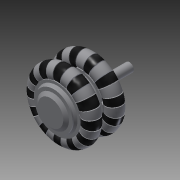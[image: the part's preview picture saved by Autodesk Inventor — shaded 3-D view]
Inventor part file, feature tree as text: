
AUTODESK INVENTOR PART (.ipt)
format: ipt  version: 2015 (Build 190159000, 159)  size: 1,335,808 bytes
history: native  units: in
note: dims shown in document units (in); Inventor stores cm internally (conversion verified against a paired STEP export)
features: sketch x14, plane x7, revolve x6, pattern_circular x3, extrude x3, mirror x1, loft x1
ambient origin geometry x8: Origin, YZ Plane, XZ Plane, XY Plane, X Axis, Y Axis, Z Axis, Center Point
bodies: Solid1 (feature_tree)
feature tree (35):
  revolve  "Revolution1"  [1 undecoded]
  revolve  "Revolution2"  [1 undecoded]
  pattern_circular  "Circular Pattern1"  Count=12 Angle=360.0deg
  sketch  "Sketch3"  dims[d7=0.0039in]
  revolve  "Revolution3"  [1 undecoded]
  sketch  "Sketch5"  dims[d9=0.0157in]
  plane  "Work Plane2"
  plane  "Work Plane6"
  revolve  "Revolution4"  Angle=360.0deg
  plane  "Work Plane4"
  revolve  "Revolution5"  [1 undecoded]
  pattern_circular  "Circular Pattern2"  [2 undecoded]
  plane  "Work Plane5"
  revolve  "Revolution6"  [1 undecoded]
  extrude  "Extrusion1"  Depth=0.0079in
  extrude  "Extrusion2"  Depth=0.3937in TaperAngle=0.0deg
  pattern_circular  "Circular Pattern3"  Count=6 Angle=360.0deg
  plane  "Work Plane7"
  mirror  "Mirror1"
  plane  "Work Plane8"
  extrude  "Extrusion3"  Depth=0.0079in
  sketch  "Sketch14"  dims[d25=0.0276in]
  plane  "Work Plane9"
  sketch  "Sketch15"  dims[d26=0.0354in]
  loft  "Loft1"
  sketch  "Sketch1"  dims[d0=0.0984in d2=0.0197in]
  sketch  "Sketch2"  dims[d5=0.0079in d6=0.0079in]
  sketch  "Sketch4"  dims[d8=90.0deg]
  sketch  "Sketch7"  dims[d10=0.0315in]
  sketch  "Sketch9"  dims[d11=15.0deg d12=4.7244in d13=360.0deg]
  sketch  "Sketch10"  dims[d15=15.0deg d17=0.0962in]
  sketch  "Sketch11"  dims[d18=0.0893in d19=4.7244in d20=360.0deg]
  sketch  "Sketch12"  dims[d22=0.0079in d23=0.0893in]
  sketch  "Sketch13"  dims[d24=0.0295in]
  sketch  "Sketch16"  dims[d27=0.0315in d28=0.3937in d29=0.0in d30=0.0276in d31=0.0079in d32=0.3937in d33=0.0in d34=2.3622in d35=360.0deg d37=0.0354in d38=0.0709in d39=0.0276in d40=0.2362in d41=0.0in d42=0.0984in d43=0.0079in d44=0.0787in d45=0.0in d46=90.0deg d47=0.0in d48=90.0deg]
note: 7 required parameter values undecoded (feature->parameter linkage not recoverable at this tier; creation-order binding heuristic only, values carry confidence <= 0.55)